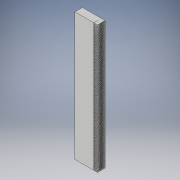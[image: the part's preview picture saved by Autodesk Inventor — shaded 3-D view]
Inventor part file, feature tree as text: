
AUTODESK INVENTOR PART (.ipt)
format: ipt  version: 2017 (Build 210142000, 142)  size: 536,576 bytes
history: native  units: in
note: dims shown in document units (in); Inventor stores cm internally (conversion verified against a paired STEP export)
features: sketch x3, extrude x2, pattern_linear x1
ambient origin geometry x8: Origin, YZ Plane, XZ Plane, XY Plane, X Axis, Y Axis, Z Axis, Center Point
bodies: Solid1 (feature_tree)
feature tree (6):
  extrude  "Extrusion1"  Depth=17.0in
  sketch  "Sketch2"  dims[d2=1.0in d3=0.0in d4=0.5in]
  extrude  "Extrusion2"  Depth=0.5in
  pattern_linear  "Rectangular Pattern2"  Count1=188 Spacing1=0.09in
  sketch  "Sketch1"  dims[d0=3.0in d1=17.0in]
  sketch  "Sketch3"  dims[d7=0.5in d8=0.0in d15=74.0157in d17=0.09in d18=0.0344in d19=0.6012in]
